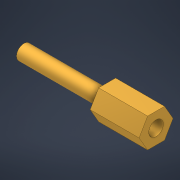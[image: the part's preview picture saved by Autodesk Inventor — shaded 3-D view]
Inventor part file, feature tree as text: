
AUTODESK INVENTOR PART (.ipt)
format: ipt  version: 2022 (Build 260153000, 153)  size: 106,496 bytes
history: native  units: in
note: dims shown in document units (in); Inventor stores cm internally (conversion verified against a paired STEP export)
features: extrude x3, sketch x3
ambient origin geometry x8: Origin, YZ Plane, XZ Plane, XY Plane, X Axis, Y Axis, Z Axis, Center Point
bodies: Solid1 (feature_tree)
feature tree (6):
  extrude  "Extrusion1"  Depth=0.3937in TaperAngle=0.0deg
  extrude  "Extrusion2"  Depth=0.6693in TaperAngle=0.0deg
  extrude  "Extrusion3"  Depth=0.2362in TaperAngle=0.0deg
  sketch  "Sketch1"  dims[d1=0.2362in d2=0.3937in d3=0.0in]
  sketch  "Sketch2"  dims[d4=0.1181in d5=0.6693in d6=0.0in]
  sketch  "Sketch3"  dims[d7=0.1181in d8=0.2362in d9=0.0in d10=0.0197in d11=0.0344in d12=0.0197in d13=0.0344in]
